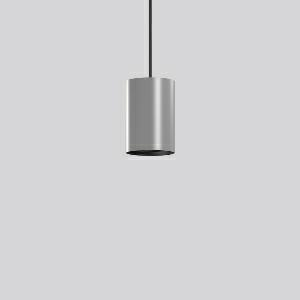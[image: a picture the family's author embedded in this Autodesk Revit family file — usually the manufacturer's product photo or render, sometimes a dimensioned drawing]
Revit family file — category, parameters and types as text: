
# Revit family: deecos_p_maxi_911541_004_76_26e0
name_source: partatom
category: Lighting Fixtures
units: mm (PartAtom-declared; Revit-internal decimal feet)

## family parameters
Cut with Voids When Loaded = No
Host = Face
Light Source = No
Part Type = Normal
Room Calculation Point = No
Round Connector Dimension = Use Diameter
Shared = No

## types (1)
- DEECOS P maxi (1 x LED Modul 930, 3500 lm, 3000)
    Apparent Load = 35 VA
    Approval mark = CE
    CIE Flux Codes = 96 100 100 100 100
    Color Rendering = 90
    Color Temperature = 3000
    Default Elevation = 1800 mm
    Description = Series: DEECOS P maxi
Cylindrical pendant luminaire. Housing: die-cast aluminium, powder-coated. Canopy made of powder-coated sheet steel with magnetic attachment. Optical assembly with lens made of plastic (polycarbonate) for the best homogeneous light distribution - can be changed without tools. Best colour rendering index Ra>90. Transparent suspension cable 2 m, can be shortened. High quality converter without flickering and stroboscopic effect. The following accessories can be mounted without use of tools: interchangeable lenses, honeycomb louvre, clear and frosted diffusers, white interchangeable plastic ring. Decorative recessed suspension set available as accessory. 
Colour: silver
Diameter: 123 mm
Height: 181 mm
Suspension length: 2000 mm
Lamp: LED
Socket: without socket
Colour temperature: 3000K
Colour rendering index (CRI): 92
System power: 35 W
Rated luminous flux: 3500 lm
Luminous efficiency: 100 lm/W
Control gear: Converter, dimmable, DALI
Protection class: I
Type of protection: IP 20
    Height = 181 mm
    Lamp = 1 x LED Modul 930
    Lamp Light Flux = 3500 lm
    Lamp count = 1
    Length = 123 mm
    Lifetime = 50000 h
    Luminous efficacy = 100 lm/W
    Manufacturer = RZB
    ModVariant = No
    Model = 911541.004.76
    Mounting Place = Ceiling
    Mounting Type = Pendant
    Number of Poles = 1
    OnlyDefault = Yes
    Power Factor = 1
    Product Name = DEECOS P maxi
    Product group = Pendant luminaires
    ProductGroupID = 902
    Protection Class = Protection class I
    Protection Degree = IP 20
    RLX_Detail_Level = 1
    RLX_Emergency_Light_Flux = 0 lm
    RLX_Emergency_Type = 0
    RLX_Emergency_Type_DB = No
    RlxData = <blob elided: 35853 chars, md5=9cd7cbba>
    Socket = socket
    Standby Power = 0 W
    System Light Flux = 3500 lm
    System Power = 35 W
    Type Comments = Product without accessories
    Type Image = 911480.004.jpg
    URL = http://relux.com
    VarID = ---
    Voltage = 230 V
    Voltage Range = 220-240 V
    Weight = 0.00 kg
    Width = 0 mm  [stored 0 ft]

note: [stored X ft] marks values corroborated as IEEE doubles in the binary element streams (Revit-internal decimal feet)

## geometry (parser evidence)
native form markers: Blend x4, Sweep x10
no freeform markers — native parametric forms only
